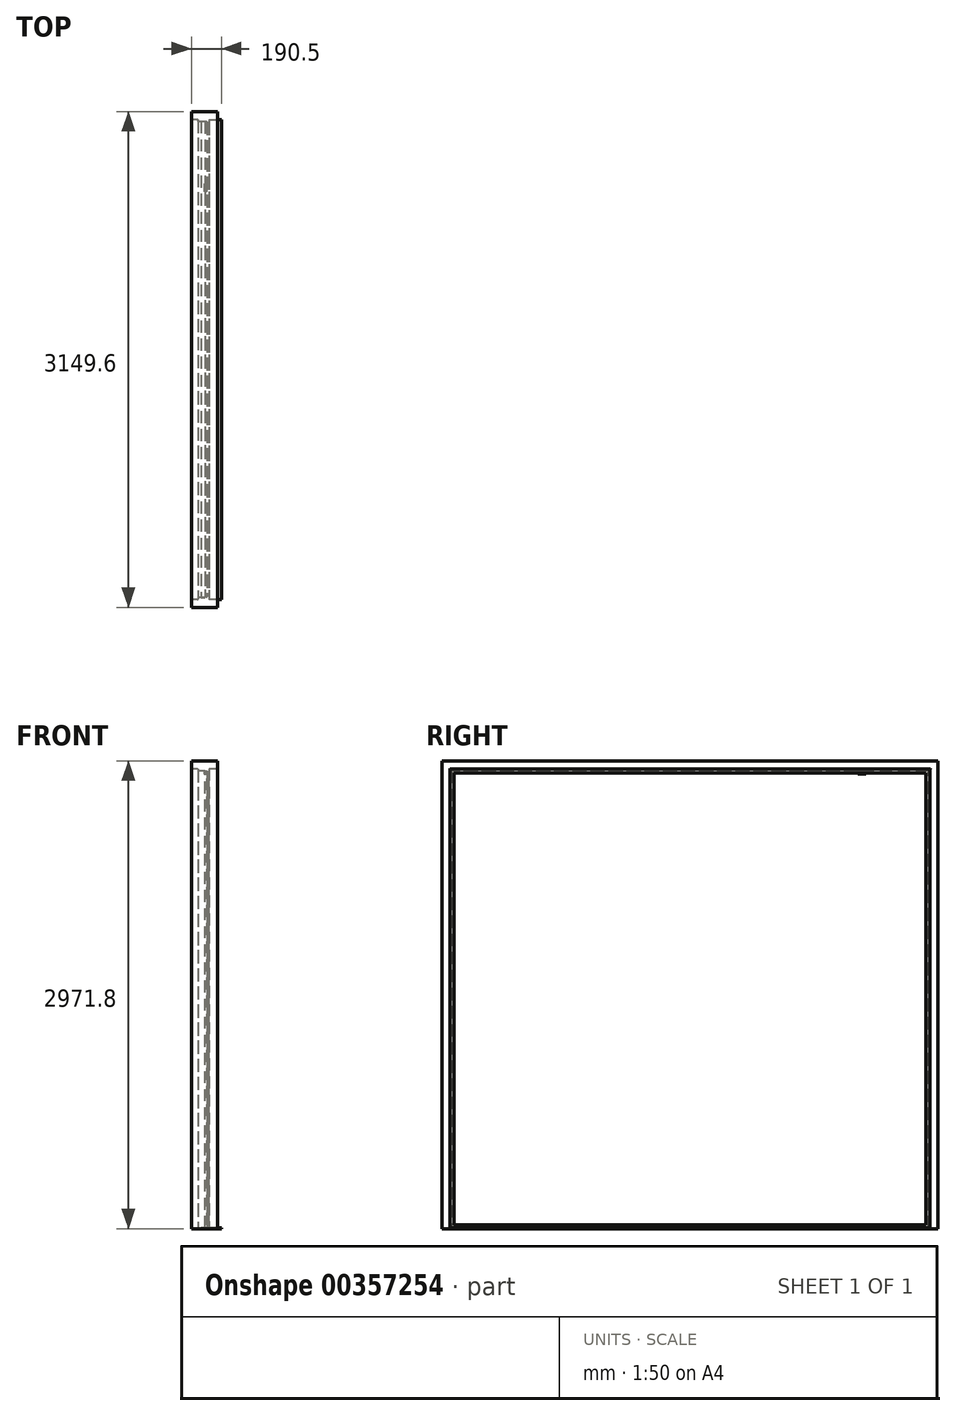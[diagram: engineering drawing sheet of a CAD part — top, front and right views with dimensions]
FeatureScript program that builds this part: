
annotation { "Feature Type Name" : "Feature", "Feature Type Description" : "" }
export const myFeature = defineFeature(function(context is Context, id is Id, definition is map)
    precondition{}
    {
        {
            var Q0;
            Q0=qCreatedBy(makeId("Top.planeOp"),FACE);
            var sketch = newSketch(context, id + "F0", { "sketchPlane" : qUnion([Q0])});
            skLineSegment(sketch, "E0", {"start": v(0, 0) * mm, "end": v(165.1, 0) * mm});
            skLineSegment(sketch, "E1", {"start": v(165.1, 0) * mm, "end": v(165.1, -50.8) * mm});
            skLineSegment(sketch, "E2", {"start": v(165.1, -50.8) * mm, "end": v(112.71, -50.8) * mm});
            skLineSegment(sketch, "E3", {"start": v(112.71, -50.8) * mm, "end": v(112.71, -76.2) * mm});
            skLineSegment(sketch, "E4", {"start": v(87.31, -63.5) * mm, "end": v(42.86, -63.5) * mm});
            skLineSegment(sketch, "E5", {"start": v(42.86, -63.5) * mm, "end": v(42.86, -50.8) * mm});
            skLineSegment(sketch, "E6", {"start": v(42.86, -50.8) * mm, "end": v(0, -50.8) * mm});
            skLineSegment(sketch, "E7", {"start": v(0, -50.8) * mm, "end": v(0, 0) * mm});
            skLineSegment(sketch, "E8", {"start": v(112.71, -76.2) * mm, "end": v(100.01, -76.2) * mm});
            skLineSegment(sketch, "E9", {"start": v(100.01, -76.2) * mm, "end": v(100.01, -66.04) * mm});
            skLineSegment(sketch, "E10", {"start": v(100.01, -66.04) * mm, "end": v(87.31, -66.04) * mm});
            skLineSegment(sketch, "E11", {"start": v(87.31, -66.04) * mm, "end": v(87.31, -63.5) * mm});
            skSolve(sketch);
        }
        {
            var Q0;
            Q0=qCreatedBy(makeId("Right.planeOp"),FACE);
            var sketch = newSketch(context, id + "F1", { "sketchPlane" : qUnion([Q0])});
            skLineSegment(sketch, "E12", {"start": v(-50.8, 0) * mm, "end": v(-50.8, 2921) * mm});
            skLineSegment(sketch, "E13", {"start": v(-50.8, 2921) * mm, "end": v(-3098.8, 2921) * mm});
            skLineSegment(sketch, "E14", {"start": v(-3098.8, 2921) * mm, "end": v(-3098.8, 0) * mm});
            skSolve(sketch);
        }
        {
            var Q0;
            Q0=makeQuery(id+"F0.imprint","IMPRINT",FACE,{"disambiguationData":[TD([[makeQuery(id+"F0.imprint","IMPRINT",EDGE,{"derivedFrom":sQuery(id+"F0.wireOp",EDGE,"E0")}),-1.0]])]});
            var Q1;
            Q1=sQuery(id+"F1.wireOp",EDGE,"E12");
            var Q2;
            Q2=sQuery(id+"F1.wireOp",EDGE,"E14");
            var Q3;
            Q3=sQuery(id+"F1.wireOp",EDGE,"E13");
            sweep(context, id + "F2", {"profiles" : qUnion([Q0]), "path" : qUnion([Q1, Q2, Q3])});
        }
        {
            var Q0;
            Q0=makeQuery(id+"F2.opSweep","SWEPT_EDGE",EDGE,{"disambiguationData":[OSD([sQuery(id+"F0.wireOp",EDGE,"E6"),sQuery(id+"F0.wireOp",EDGE,"E7"),sQuery(id+"F1.wireOp",EDGE,"E12")])]});
            var Q1;
            Q1=makeQuery(id+"F2.opSweep","SWEPT_EDGE",EDGE,{"disambiguationData":[OSD([sQuery(id+"F0.wireOp",EDGE,"E5"),sQuery(id+"F0.wireOp",EDGE,"E6"),sQuery(id+"F1.wireOp",EDGE,"E12")])]});
            var Q2;
            Q2=makeQuery(id+"F2.opSweep","SWEPT_EDGE",EDGE,{"disambiguationData":[OSD([sQuery(id+"F0.wireOp",EDGE,"E4"),sQuery(id+"F0.wireOp",EDGE,"E5"),sQuery(id+"F1.wireOp",EDGE,"E12")])]});
            var Q3;
            Q3=makeQuery(id+"F2.opSweep","SWEPT_EDGE",EDGE,{"disambiguationData":[OSD([sQuery(id+"F0.wireOp",EDGE,"E1"),sQuery(id+"F0.wireOp",EDGE,"E2"),sQuery(id+"F1.wireOp",EDGE,"E12")])]});
            var Q4;
            Q4=makeQuery(id+"F2.opSweep","SWEPT_EDGE",EDGE,{"disambiguationData":[OSD([sQuery(id+"F0.wireOp",EDGE,"E1"),sQuery(id+"F0.wireOp",EDGE,"E2"),sQuery(id+"F1.wireOp",EDGE,"E13")])]});
            var Q5;
            Q5=makeQuery(id+"F2.opSweep","SWEPT_EDGE",EDGE,{"disambiguationData":[OSD([sQuery(id+"F0.wireOp",EDGE,"E6"),sQuery(id+"F0.wireOp",EDGE,"E7"),sQuery(id+"F1.wireOp",EDGE,"E13")])]});
            var Q6;
            Q6=makeQuery(id+"F2.opSweep","SWEPT_EDGE",EDGE,{"disambiguationData":[OSD([sQuery(id+"F0.wireOp",EDGE,"E5"),sQuery(id+"F0.wireOp",EDGE,"E6"),sQuery(id+"F1.wireOp",EDGE,"E13")])]});
            var Q7;
            Q7=makeQuery(id+"F2.opSweep","SWEPT_EDGE",EDGE,{"disambiguationData":[OSD([sQuery(id+"F0.wireOp",EDGE,"E4"),sQuery(id+"F0.wireOp",EDGE,"E5"),sQuery(id+"F1.wireOp",EDGE,"E13")])]});
            var Q8;
            Q8=makeQuery(id+"F2.opSweep","SWEPT_EDGE",EDGE,{"disambiguationData":[OSD([sQuery(id+"F0.wireOp",EDGE,"E6"),sQuery(id+"F0.wireOp",EDGE,"E7"),sQuery(id+"F1.wireOp",EDGE,"E14")])]});
            var Q9;
            Q9=makeQuery(id+"F2.opSweep","SWEPT_EDGE",EDGE,{"disambiguationData":[OSD([sQuery(id+"F0.wireOp",EDGE,"E5"),sQuery(id+"F0.wireOp",EDGE,"E6"),sQuery(id+"F1.wireOp",EDGE,"E14")])]});
            var Q10;
            Q10=makeQuery(id+"F2.opSweep","SWEPT_EDGE",EDGE,{"disambiguationData":[OSD([sQuery(id+"F0.wireOp",EDGE,"E4"),sQuery(id+"F0.wireOp",EDGE,"E5"),sQuery(id+"F1.wireOp",EDGE,"E14")])]});
            var Q11;
            Q11=makeQuery(id+"F2.opSweep","SWEPT_EDGE",EDGE,{"disambiguationData":[OSD([sQuery(id+"F0.wireOp",EDGE,"E9"),sQuery(id+"F0.wireOp",EDGE,"E10"),sQuery(id+"F1.wireOp",EDGE,"E14")])]});
            var Q12;
            Q12=makeQuery(id+"F2.opSweep","SWEPT_EDGE",EDGE,{"disambiguationData":[OSD([sQuery(id+"F0.wireOp",EDGE,"E9"),sQuery(id+"F0.wireOp",EDGE,"E10"),sQuery(id+"F1.wireOp",EDGE,"E13")])]});
            var Q13;
            Q13=makeQuery(id+"F2.opSweep","SWEPT_EDGE",EDGE,{"disambiguationData":[OSD([sQuery(id+"F0.wireOp",EDGE,"E9"),sQuery(id+"F0.wireOp",EDGE,"E10"),sQuery(id+"F1.wireOp",EDGE,"E12")])]});
            fillet(context, id + "F3", {"entities" : qUnion([Q0, Q1, Q2, Q3, Q4, Q5, Q6, Q7, Q8, Q9, Q10, Q11, Q12, Q13]), "radius" : 1.9 * mm, "tangentPropagation" : true, "allowEdgeOverflow" : false});
        }
        {
            var Q0;
            Q0=makeQuery(id+"F2.opSweep","SWEPT_FACE",FACE,{"disambiguationData":[OSD([sQuery(id+"F0.wireOp",EDGE,"E0"),sQuery(id+"F1.wireOp",EDGE,"E14")])]});
            var Q1;
            Q1=makeQuery(id+"F2.opSweep","SWEPT_FACE",FACE,{"disambiguationData":[OSD([sQuery(id+"F0.wireOp",EDGE,"E0"),sQuery(id+"F1.wireOp",EDGE,"E12")])]});
            cPlane(context, id + "F4", {"entities" : qUnion([Q0, Q1]), "cplaneType" : CPlaneType.MID_PLANE, "offset" : 25.4 * mm, "width" : 152.4 * mm, "height" : 152.4 * mm});
        }
        {
            var Q0;
            Q0=qCreatedBy(id+"F4.planeOp",FACE);
            var sketch = newSketch(context, id + "F5", { "sketchPlane" : qUnion([Q0])});
            skLineSegment(sketch, "E15", {"start": v(63.5, 0) * mm, "end": v(190.5, 0) * mm});
            skLineSegment(sketch, "E16", {"start": v(190.5, 0) * mm, "end": v(190.5, 3.8) * mm});
            skLineSegment(sketch, "E17", {"start": v(190.5, 3.8) * mm, "end": v(112.71, 6.35) * mm});
            skLineSegment(sketch, "E18", {"start": v(112.71, 6.35) * mm, "end": v(112.71, 25.4) * mm});
            skLineSegment(sketch, "E19", {"start": v(112.71, 25.4) * mm, "end": v(100.01, 25.4) * mm});
            skLineSegment(sketch, "E20", {"start": v(100.01, 25.4) * mm, "end": v(100.01, 6.35) * mm});
            skLineSegment(sketch, "E21", {"start": v(100.01, 6.35) * mm, "end": v(63.5, 3.8) * mm});
            skLineSegment(sketch, "E22", {"start": v(63.5, 3.8) * mm, "end": v(63.5, 0) * mm});
            skSolve(sketch);
        }
        {
            var Q0;
            Q0=makeQuery(id+"F5.imprint","IMPRINT",FACE,{"disambiguationData":[TD([[makeQuery(id+"F5.imprint","IMPRINT",EDGE,{"derivedFrom":sQuery(id+"F5.wireOp",EDGE,"E15")}),1.0]])]});
            var Q1;
            Q1=makeQuery(id+"F2.opSweep","SWEPT_FACE",FACE,{"disambiguationData":[OSD([sQuery(id+"F0.wireOp",EDGE,"E2"),sQuery(id+"F1.wireOp",EDGE,"E12")])]});
            var Q2;
            Q2=makeQuery(id+"F2.opSweep","SWEPT_FACE",FACE,{"disambiguationData":[OSD([sQuery(id+"F0.wireOp",EDGE,"E2"),sQuery(id+"F1.wireOp",EDGE,"E14")])]});
            extrude(context, id + "F6", {"entities" : qUnion([Q0]), "operationType" : NewBodyOperationType.ADD, "endBound" : BoundingType.UP_TO_SURFACE, "oppositeDirection" : true, "endBoundEntityFace" : qUnion([Q1]), "depth" : 25.4 * mm, "hasSecondDirection" : true, "secondDirectionBound" : SecondDirectionBoundingType.UP_TO_SURFACE, "secondDirectionOppositeDirection" : false, "secondDirectionBoundEntityFace" : qUnion([Q2]), "secondDirectionDepth" : 25.4 * mm});
        }
        {
            var Q0;
            Q0=makeQuery(id+"F2.opSweep","SWEPT_FACE",FACE,{"disambiguationData":[OSD([sQuery(id+"F0.wireOp",EDGE,"E10"),sQuery(id+"F1.wireOp",EDGE,"E13")])]});
            var sketch = newSketch(context, id + "F7", { "sketchPlane" : qUnion([Q0])});
            skLineSegment(sketch, "E23.right", {"start": v(98.1, 457.2) * mm, "end": v(98.1, 508) * mm});
            skLineSegment(sketch, "E24", {"start": v(98.1, 508) * mm, "end": v(85.4, 508) * mm});
            skLineSegment(sketch, "E25", {"start": v(85.4, 508) * mm, "end": v(85.4, 457.2) * mm});
            skLineSegment(sketch, "E26", {"start": v(85.4, 457.2) * mm, "end": v(98.1, 457.2) * mm});
            skSolve(sketch);
        }
        {
            var Q0;
            Q0 = qSketchRegion(id + "F7", true);
            extrude(context, id + "F8", {"entities" : qUnion([Q0]), "operationType" : NewBodyOperationType.ADD, "depth" : 19.05 * mm});
        }
    });
